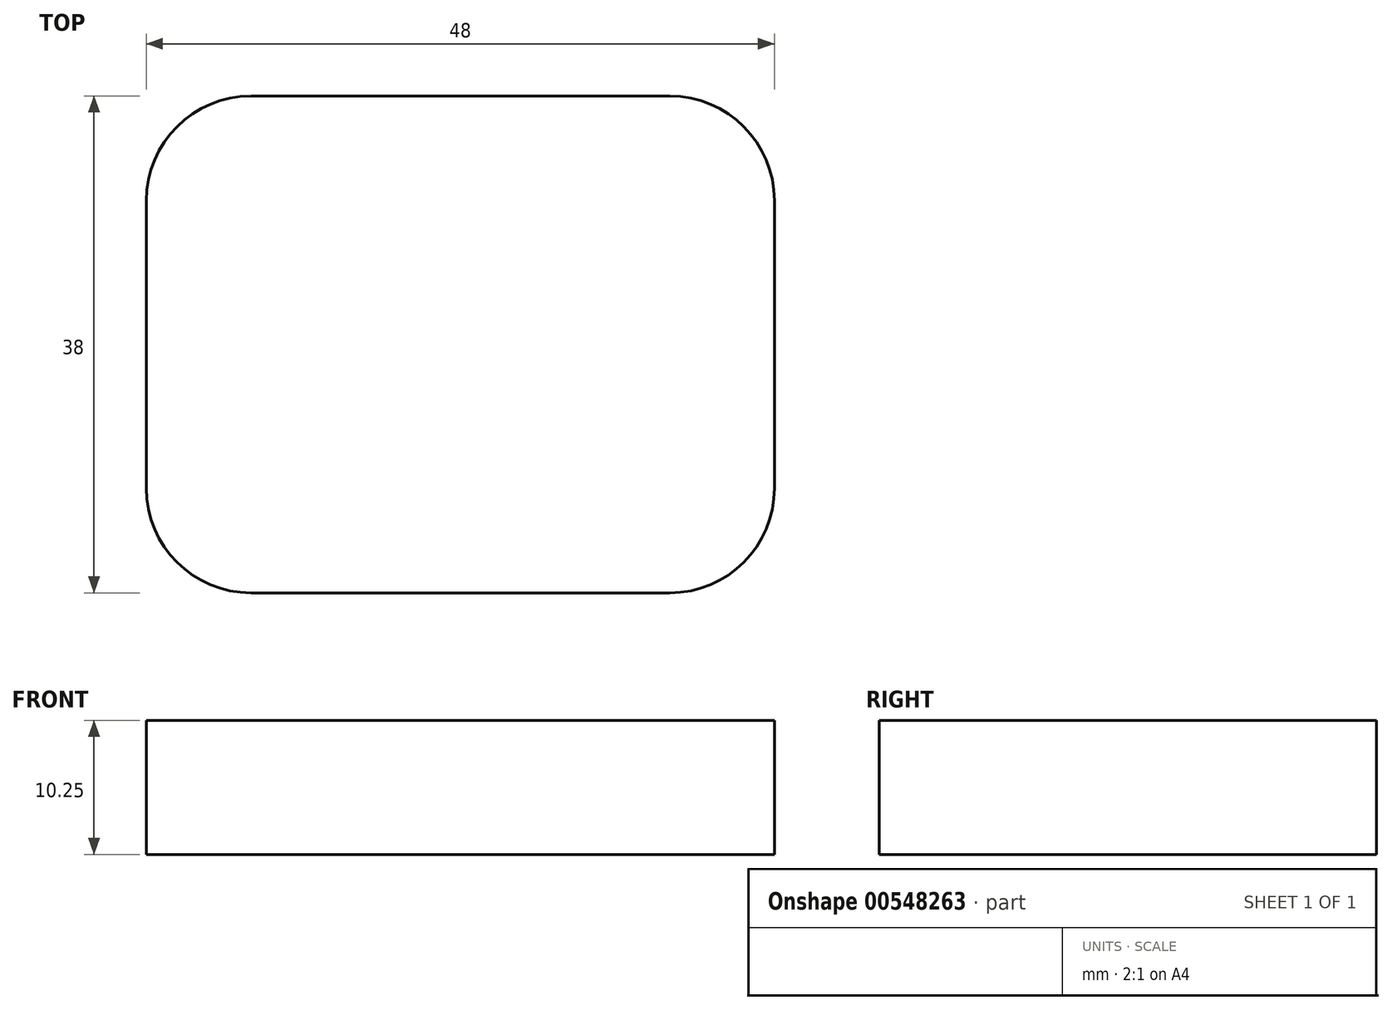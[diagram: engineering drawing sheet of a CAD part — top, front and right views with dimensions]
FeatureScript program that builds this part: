
annotation { "Feature Type Name" : "Feature", "Feature Type Description" : "" }
export const myFeature = defineFeature(function(context is Context, id is Id, definition is map)
    precondition{}
    {
        {
            var Q0;
            Q0=qCreatedBy(makeId("Top.planeOp"),FACE);
            var sketch = newSketch(context, id + "F0", { "sketchPlane" : qUnion([Q0])});
            skLineSegment(sketch, "E0.bottom", {"start": v(-16, 19) * mm, "end": v(16, 19) * mm});
            skLineSegment(sketch, "E0.top", {"start": v(-16, -19) * mm, "end": v(16, -19) * mm});
            skLineSegment(sketch, "E0.left", {"start": v(-24, 11) * mm, "end": v(-24, -11) * mm});
            skLineSegment(sketch, "E0.right", {"start": v(24, 11) * mm, "end": v(24, -11) * mm});
            skPoint(sketch, "E1.visualSharp", {"position": v(-24, 19) * mm});
            skArc(sketch, "E1.filletArc", {"start": v(-16, 19) * mm, "mid": v(-21.66, 16.66) * mm, "end": v(-24, 11) * mm});
            skPoint(sketch, "E2.visualSharp", {"position": v(24, 19) * mm});
            skArc(sketch, "E2.filletArc", {"start": v(24, 11) * mm, "mid": v(21.66, 16.66) * mm, "end": v(16, 19) * mm});
            skPoint(sketch, "E3.visualSharp", {"position": v(24, -19) * mm});
            skArc(sketch, "E3.filletArc", {"start": v(16, -19) * mm, "mid": v(21.66, -16.66) * mm, "end": v(24, -11) * mm});
            skPoint(sketch, "E4.visualSharp", {"position": v(-24, -19) * mm});
            skArc(sketch, "E4.filletArc", {"start": v(-24, -11) * mm, "mid": v(-21.66, -16.66) * mm, "end": v(-16, -19) * mm});
            skSolve(sketch);
        }
        {
            var Q0;
            Q0=makeQuery(id+"F0.imprint","IMPRINT",FACE,{"disambiguationData":[TD([[makeQuery(id+"F0.imprint","IMPRINT",EDGE,{"derivedFrom":sQuery(id+"F0.wireOp",EDGE,"E0.bottom")}),-1.0]])]});
            extrude(context, id + "F1", {"entities" : qUnion([Q0]), "depth" : 10.25 * mm, "offsetDistance" : 25 * mm});
        }
    });
